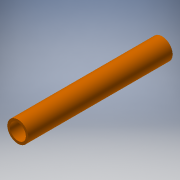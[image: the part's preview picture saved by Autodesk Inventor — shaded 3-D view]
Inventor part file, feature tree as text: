
AUTODESK INVENTOR PART (.ipt)
format: ipt  version: 2018.2 (Build 222227000, 227)  size: 109,568 bytes
history: native  units: in
note: dims shown in document units (in); Inventor stores cm internally (conversion verified against a paired STEP export)
features: extrude x1, sketch x1
ambient origin geometry x8: Origin, YZ Plane, XZ Plane, XY Plane, X Axis, Y Axis, Z Axis, Center Point
bodies: Solid1 (feature_tree)
feature tree (2):
  extrude  "Extrusion1"  Depth=9.0in
  sketch  "Sketch1"  dims[d0=1.315in d1=1.0in d2=9.0in d3=0.0in]
